# Revit family: Mount_RigidRail_Kattsafe_Purlin_Inline
name_source: partatom
category: Specialty Equipment
units: mm (PartAtom-declared; Revit-internal decimal feet)

## family parameters
Always vertical = Yes
Cut with Voids When Loaded = No
Enable Cutting in Views = No
Maintain Annotation Orientation = No
OmniClass Number = 23.27.71.21
Part Type = Normal
Room Calculation Point = No
Round Connector Dimension = Use Diameter
Shared = No
Work Plane-Based = No

## types (2) — shared parameters
Assembly Code = E1090100
Description = Rigid rails provide significant spanning capabilities, making them very versatile where there are limited support structures. The high strength aluminium construction, along with the unique t-bolt assembly makes it a very simple and easily adaptable system to install.
Export Type to IFC As = IfcBuildingElementProxy
IfcExportAs = IfcBuildingElementProxy
IfcExportType = USERDEFINED
Manufacturer = Kattsafe®
ManufacturerOverallDepth = 400 mm  [stored 1.31234 ft]
ManufacturerURLProductSpecific = https://kattsafe.com.au
Material = Steel_Stainless_Kattsafe_Satin
ModifiedIssue = 20240430 $
Type IFC Predefined Type = USERDEFINED
URL = https://kattsafe.com.au
Uniclass2015Code = Pr_20_85_09
Uniclass2015Title = Brackets
Uniclass2015Version = Products v1.23
zero-valued in all types: Default Elevation

## per-type parameters (varying)
| type | 3mPurlinSpreader | 4mPurlinSpreader | ManufacturerOverallWidth | ManufacturerSpecCode | Model | PurlinSpreaderLength | Type Comments |
| 3.0M Purlin Spreader (OH277) | Yes | No | 3000 mm  [stored 9.84252 ft] | OH277 | OH277 | 3000 mm  [stored 9.84252 ft] | Purlin Spreader with Suspension Kit - 3.0M |
| 4.0M Purlin Spreader (OH278) | No | Yes | 4000 mm  [stored 13.1234 ft] | OH278 | OH278 | 4000 mm  [stored 13.1234 ft] | Purlin Spreader with Suspension Kit - 4.0M |

note: [stored X ft] marks values corroborated as IEEE doubles in the binary element streams (Revit-internal decimal feet)

## geometry (parser evidence)
native form markers: Sweep x5
no freeform markers — native parametric forms only
